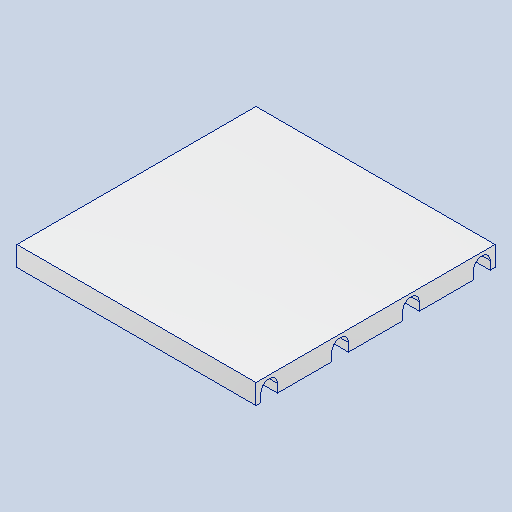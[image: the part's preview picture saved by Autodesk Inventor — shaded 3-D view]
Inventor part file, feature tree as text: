
AUTODESK INVENTOR PART (.ipt)
format: ipt  version: 2022 (Build 260153000, 153)  size: 125,440 bytes
history: native  units: in
note: dims shown in document units (in); Inventor stores cm internally (conversion verified against a paired STEP export)
features: extrude x2, sketch x2
ambient origin geometry x8: Origin, YZ Plane, XZ Plane, XY Plane, X Axis, Y Axis, Z Axis, Center Point
bodies: Solid1 (feature_tree)
feature tree (4):
  extrude  "Extrusion1"  Depth=12.0in
  extrude  "Extrusion2"  Depth=0.42in
  sketch  "Sketch1"  dims[d0=12.0in d1=12.0in]
  sketch  "Sketch2"  dims[d2=1.0in d3=0.0in d4=0.42in d5=0.42in d6=0.24in d7=0.42in d8=1.5748in d10=3.56in d11=0.3937in d13=1.0in d15=0.24in d16=0.0in d17=0.0in]
